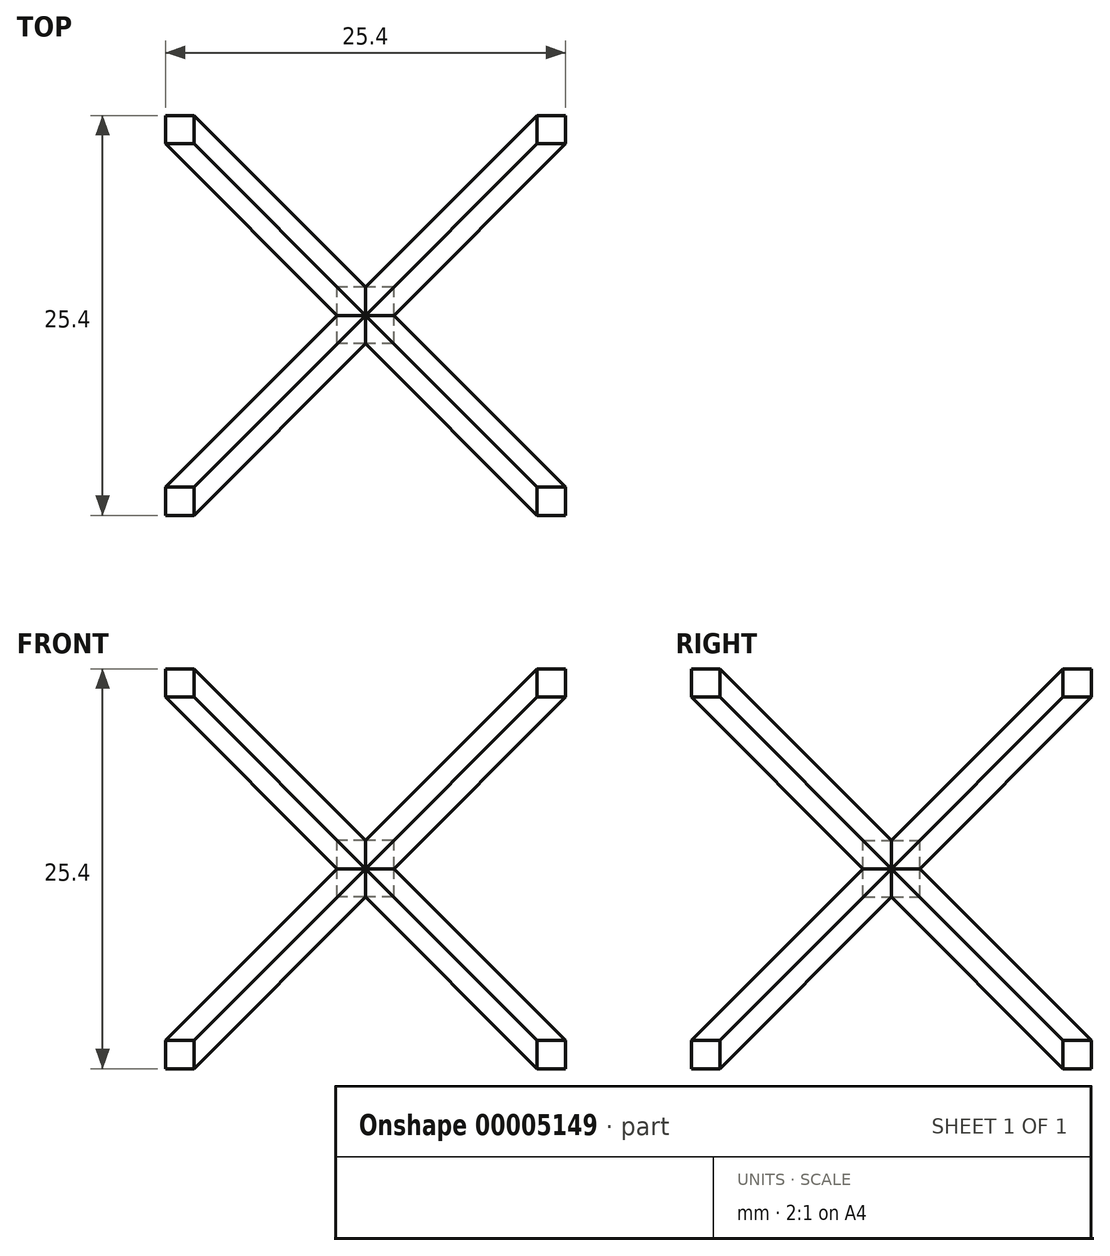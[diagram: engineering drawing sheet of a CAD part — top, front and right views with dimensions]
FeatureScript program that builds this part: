
annotation { "Feature Type Name" : "Feature", "Feature Type Description" : "" }
export const myFeature = defineFeature(function(context is Context, id is Id, definition is map)
    precondition{}
    {
        {
            var Q0;
            Q0=qCreatedBy(makeId("Front.planeOp"),FACE);
            var sketch = newSketch(context, id + "F0", { "sketchPlane" : qUnion([Q0])});
            skLineSegment(sketch, "E0", {"start": v(0, 0) * mm, "end": v(12.7, 12.7) * mm});
            skLineSegment(sketch, "E1", {"start": v(12.7, 12.7) * mm, "end": v(12.7, 10.9) * mm});
            skLineSegment(sketch, "E2", {"start": v(12.7, -12.7) * mm, "end": v(0, 0) * mm});
            skLineSegment(sketch, "E3.0", {"start": v(1.8, 0) * mm, "end": v(12.7, 10.9) * mm});
            skLineSegment(sketch, "E3.1", {"start": v(12.7, -10.9) * mm, "end": v(1.8, 0) * mm});
            skLineSegment(sketch, "E4.trimOffspring", {"start": v(12.7, -10.9) * mm, "end": v(12.7, -12.7) * mm});
            skSolve(sketch);
        }
        {
            var Q0;
            Q0=makeQuery(id+"F0.imprint","IMPRINT",FACE,{"disambiguationData":[TD([[makeQuery(id+"F0.imprint","IMPRINT",EDGE,{"derivedFrom":sQuery(id+"F0.wireOp",EDGE,"E0")}),-1.0]])]});
            extrude(context, id + "F1", {"entities" : qUnion([Q0]), "depth" : 25.4 * mm});
        }
        {
            var Q0;
            Q0=makeQuery(id+"F1.opExtrude","SWEPT_BODY",BODY,{"disambiguationData":[OSD([sQuery(id+"F0.wireOp",EDGE,"E0"),sQuery(id+"F0.wireOp",EDGE,"E1"),sQuery(id+"F0.wireOp",EDGE,"E2"),sQuery(id+"F0.wireOp",EDGE,"E3.0"),sQuery(id+"F0.wireOp",EDGE,"E3.1"),sQuery(id+"F0.wireOp",EDGE,"E3.2")])]});
            var Q1;
            Q1=makeQuery(id+"F1.opExtrude","SWEPT_EDGE",EDGE,{"disambiguationData":[OSD([sQuery(id+"F0.wireOp",EDGE,"E0"),sQuery(id+"F0.wireOp",EDGE,"E2")])]});
            circularPattern(context, id + "F2", {"entities" : qUnion([Q0]), "axis" : qUnion([Q1]), "angle" : 90 * degree, "instanceCount" : 4, "computeTransformsWithoutBuiltin" : true});
        }
        {
            var Q0;
            Q0=makeQuery(id+"F1.opExtrude","SWEPT_BODY",BODY,{"disambiguationData":[OSD([sQuery(id+"F0.wireOp",EDGE,"E0"),sQuery(id+"F0.wireOp",EDGE,"E1"),sQuery(id+"F0.wireOp",EDGE,"E2"),sQuery(id+"F0.wireOp",EDGE,"E3.0"),sQuery(id+"F0.wireOp",EDGE,"E3.1"),sQuery(id+"F0.wireOp",EDGE,"E3.2")])]});
            var Q1;
            Q1=makeQuery(id+"F2.opPattern","COPY",BODY,{"derivedFrom":makeQuery(id+"F1.opExtrude","SWEPT_BODY",BODY,{"disambiguationData":[OSD([sQuery(id+"F0.wireOp",EDGE,"E0"),sQuery(id+"F0.wireOp",EDGE,"E1"),sQuery(id+"F0.wireOp",EDGE,"E2"),sQuery(id+"F0.wireOp",EDGE,"E3.0"),sQuery(id+"F0.wireOp",EDGE,"E3.1"),sQuery(id+"F0.wireOp",EDGE,"E3.2")])]}),"instanceName":"1"});
            var Q2;
            Q2=makeQuery(id+"F2.opPattern","COPY",BODY,{"derivedFrom":makeQuery(id+"F1.opExtrude","SWEPT_BODY",BODY,{"disambiguationData":[OSD([sQuery(id+"F0.wireOp",EDGE,"E0"),sQuery(id+"F0.wireOp",EDGE,"E1"),sQuery(id+"F0.wireOp",EDGE,"E2"),sQuery(id+"F0.wireOp",EDGE,"E3.0"),sQuery(id+"F0.wireOp",EDGE,"E3.1"),sQuery(id+"F0.wireOp",EDGE,"E3.2")])]}),"instanceName":"2"});
            var Q3;
            Q3=makeQuery(id+"F2.opPattern","COPY",BODY,{"derivedFrom":makeQuery(id+"F1.opExtrude","SWEPT_BODY",BODY,{"disambiguationData":[OSD([sQuery(id+"F0.wireOp",EDGE,"E0"),sQuery(id+"F0.wireOp",EDGE,"E1"),sQuery(id+"F0.wireOp",EDGE,"E2"),sQuery(id+"F0.wireOp",EDGE,"E3.0"),sQuery(id+"F0.wireOp",EDGE,"E3.1"),sQuery(id+"F0.wireOp",EDGE,"E3.2")])]}),"instanceName":"3"});
            booleanBodies(context, id + "F3", {"operationType" : BooleanOperationType.UNION, "tools" : qUnion([Q0, Q1, Q2, Q3])});
        }
        {
            var Q0;
            Q0=makeQuery(id+"F1.opExtrude","SWEPT_BODY",BODY,{"disambiguationData":[OSD([sQuery(id+"F0.wireOp",EDGE,"E0"),sQuery(id+"F0.wireOp",EDGE,"E1"),sQuery(id+"F0.wireOp",EDGE,"E2"),sQuery(id+"F0.wireOp",EDGE,"E3.0"),sQuery(id+"F0.wireOp",EDGE,"E3.1"),sQuery(id+"F0.wireOp",EDGE,"E3.2")])]});
            var Q1;
            Q1=makeQuery(id+"F2.opPattern","COPY",EDGE,{"derivedFrom":makeQuery(id+"F1.opExtrude","CAP_EDGE",EDGE,{"disambiguationData":[OSD([sQuery(id+"F0.wireOp",EDGE,"E1")])],"isStart":false}),"instanceName":"2"});
            transform(context, id + "F4", {"entities" : qUnion([Q0]), "transformType" : TransformType.ROTATION, "transformAxis" : qUnion([Q1]), "angle" : 90 * degree, "makeCopy" : true});
        }
        {
            var Q0;
            Q0=makeQuery(id+"F4.opPattern","COPY",BODY,{"derivedFrom":makeQuery(id+"F1.opExtrude","SWEPT_BODY",BODY,{"disambiguationData":[OSD([sQuery(id+"F0.wireOp",EDGE,"E0"),sQuery(id+"F0.wireOp",EDGE,"E1"),sQuery(id+"F0.wireOp",EDGE,"E2"),sQuery(id+"F0.wireOp",EDGE,"E3.0"),sQuery(id+"F0.wireOp",EDGE,"E3.1"),sQuery(id+"F0.wireOp",EDGE,"E3.2")])]}),"instanceName":"1"});
            var Q1;
            {var subQ0=sQuery(id+"F0.wireOp",EDGE,"E1");Q1=makeQuery(id+"F4.opPattern","COPY",EDGE,{"derivedFrom":makeQuery(id+"F3.opBoolean","MERGE",EDGE,{"derivedFrom":[makeQuery(id+"F2.opPattern","COPY",EDGE,{"derivedFrom":makeQuery(id+"F1.opExtrude","SWEPT_EDGE",EDGE,{"disambiguationData":[OSD([subQ0,sQuery(id+"F0.wireOp",EDGE,"E2")])]}),"instanceName":"2"}),makeQuery(id+"F2.opPattern","COPY",EDGE,{"derivedFrom":makeQuery(id+"F1.opExtrude","SWEPT_EDGE",EDGE,{"disambiguationData":[OSD([sQuery(id+"F0.wireOp",EDGE,"E0"),subQ0])]}),"instanceName":"3"})]}),"instanceName":"1"});}
            transform(context, id + "F5", {"entities" : qUnion([Q0]), "transformType" : TransformType.TRANSLATION_ENTITY, "oppositeDirectionEntity" : true, "transformLine" : qUnion([Q1]), "makeCopy" : false});
        }
        {
            var Q0;
            Q0=makeQuery(id+"F1.opExtrude","SWEPT_BODY",BODY,{"disambiguationData":[OSD([sQuery(id+"F0.wireOp",EDGE,"E0"),sQuery(id+"F0.wireOp",EDGE,"E1"),sQuery(id+"F0.wireOp",EDGE,"E2"),sQuery(id+"F0.wireOp",EDGE,"E3.0"),sQuery(id+"F0.wireOp",EDGE,"E3.1"),sQuery(id+"F0.wireOp",EDGE,"E3.2")])]});
            var Q1;
            Q1=makeQuery(id+"F2.opPattern","COPY",EDGE,{"derivedFrom":makeQuery(id+"F1.opExtrude","CAP_EDGE",EDGE,{"disambiguationData":[OSD([sQuery(id+"F0.wireOp",EDGE,"E1")])],"isStart":false}),"instanceName":"3"});
            transform(context, id + "F6", {"entities" : qUnion([Q0]), "transformType" : TransformType.ROTATION, "transformAxis" : qUnion([Q1]), "angle" : 90 * degree, "makeCopy" : true});
        }
        {
            var Q0;
            Q0=makeQuery(id+"F6.opPattern","COPY",BODY,{"derivedFrom":makeQuery(id+"F1.opExtrude","SWEPT_BODY",BODY,{"disambiguationData":[OSD([sQuery(id+"F0.wireOp",EDGE,"E0"),sQuery(id+"F0.wireOp",EDGE,"E1"),sQuery(id+"F0.wireOp",EDGE,"E2"),sQuery(id+"F0.wireOp",EDGE,"E3.0"),sQuery(id+"F0.wireOp",EDGE,"E3.1"),sQuery(id+"F0.wireOp",EDGE,"E3.2")])]}),"instanceName":"1"});
            var Q1;
            {var subQ0=sQuery(id+"F0.wireOp",EDGE,"E1");Q1=makeQuery(id+"F6.opPattern","COPY",EDGE,{"derivedFrom":makeQuery(id+"F3.opBoolean","MERGE",EDGE,{"derivedFrom":[makeQuery(id+"F1.opExtrude","SWEPT_EDGE",EDGE,{"disambiguationData":[OSD([sQuery(id+"F0.wireOp",EDGE,"E0"),subQ0])]}),makeQuery(id+"F2.opPattern","COPY",EDGE,{"derivedFrom":makeQuery(id+"F1.opExtrude","SWEPT_EDGE",EDGE,{"disambiguationData":[OSD([subQ0,sQuery(id+"F0.wireOp",EDGE,"E2")])]}),"instanceName":"3"})]}),"instanceName":"1"});}
            transform(context, id + "F7", {"entities" : qUnion([Q0]), "transformType" : TransformType.TRANSLATION_ENTITY, "oppositeDirectionEntity" : true, "transformLine" : qUnion([Q1]), "makeCopy" : false});
        }
        {
            var Q0;
            Q0=makeQuery(id+"F1.opExtrude","SWEPT_BODY",BODY,{"disambiguationData":[OSD([sQuery(id+"F0.wireOp",EDGE,"E0"),sQuery(id+"F0.wireOp",EDGE,"E1"),sQuery(id+"F0.wireOp",EDGE,"E2"),sQuery(id+"F0.wireOp",EDGE,"E3.0"),sQuery(id+"F0.wireOp",EDGE,"E3.1"),sQuery(id+"F0.wireOp",EDGE,"E3.2")])]});
            var Q1;
            Q1=makeQuery(id+"F6.opPattern","COPY",BODY,{"derivedFrom":makeQuery(id+"F1.opExtrude","SWEPT_BODY",BODY,{"disambiguationData":[OSD([sQuery(id+"F0.wireOp",EDGE,"E0"),sQuery(id+"F0.wireOp",EDGE,"E1"),sQuery(id+"F0.wireOp",EDGE,"E2"),sQuery(id+"F0.wireOp",EDGE,"E3.0"),sQuery(id+"F0.wireOp",EDGE,"E3.1"),sQuery(id+"F0.wireOp",EDGE,"E3.2")])]}),"instanceName":"1"});
            var Q2;
            Q2=makeQuery(id+"F4.opPattern","COPY",BODY,{"derivedFrom":makeQuery(id+"F1.opExtrude","SWEPT_BODY",BODY,{"disambiguationData":[OSD([sQuery(id+"F0.wireOp",EDGE,"E0"),sQuery(id+"F0.wireOp",EDGE,"E1"),sQuery(id+"F0.wireOp",EDGE,"E2"),sQuery(id+"F0.wireOp",EDGE,"E3.0"),sQuery(id+"F0.wireOp",EDGE,"E3.1"),sQuery(id+"F0.wireOp",EDGE,"E3.2")])]}),"instanceName":"1"});
            booleanBodies(context, id + "F8", {"operationType" : BooleanOperationType.INTERSECTION, "tools" : qUnion([Q0, Q1, Q2])});
        }
    });
